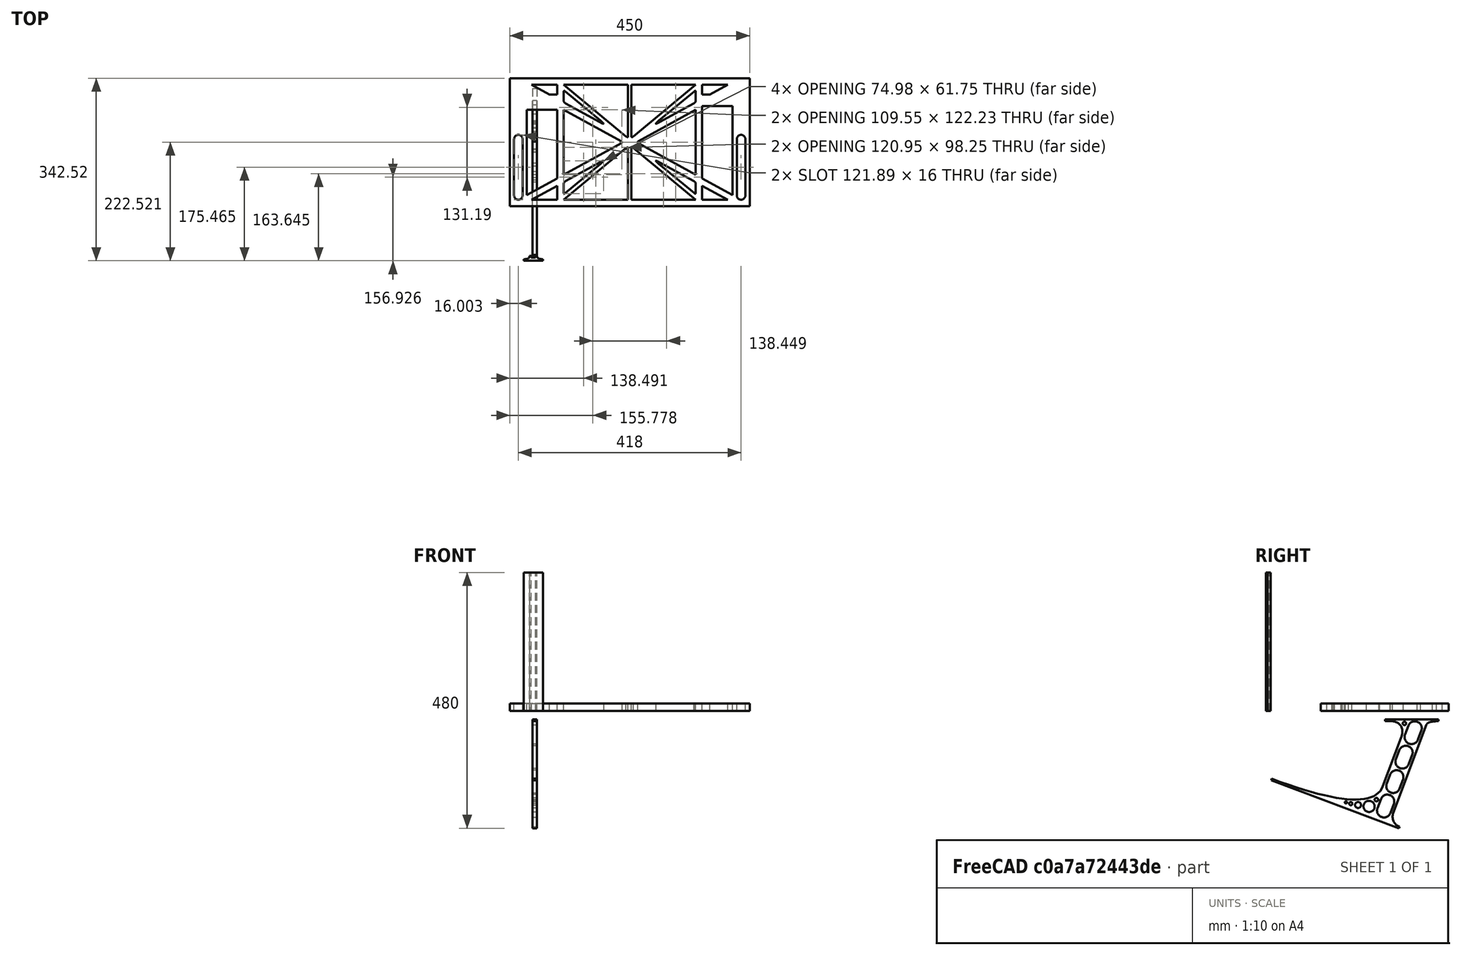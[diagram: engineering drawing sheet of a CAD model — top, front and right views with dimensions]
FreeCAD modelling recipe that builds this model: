
FCSTD DOCUMENT  (FreeCAD 0.19R0.19.2)
Label: laptopStand076
License: All rights reserved
LicenseURL: http://en.wikipedia.org/wiki/All_rights_reserved
objects: Sketcher::SketchObject×3, Part::Extrusion×3
note: 6 computed .brp shape members not serialized (recipe doc carries the construction recipe); baked Part::Feature solids carry a one-line shape summary decoded from their .brp

FEATURE [Sketcher::SketchObject] Sketch
  FullyConstrained = false
  sketch-geometry (176):
    g0: LineSegment StartX=-10.9272 StartY=-82.7794 StartZ=0 EndX=46.0728 EndY=-51.4823 EndZ=0
    g1: LineSegment StartX=366.073 StartY=-91.7794 StartZ=0 EndX=318.073 EndY=-65.424 EndZ=0
    g2: LineSegment StartX=-10.9272 StartY=77.3346 StartZ=0 EndX=-10.9272 EndY=-82.7794 EndZ=0
    g3: LineSegment StartX=375.073 StartY=-82.7794 StartZ=0 EndX=375.073 EndY=83.9235 EndZ=0
    g4: LineSegment StartX=-1.92719 StartY=-91.7794 StartZ=0 EndX=46.0728 EndY=-91.7794 EndZ=0
    g5: LineSegment StartX=318.073 StartY=124.221 StartZ=0 EndX=366.073 EndY=124.221 EndZ=0
    g6: LineSegment StartX=306.073 StartY=124.221 StartZ=0 EndX=189.124 EndY=27.0628 EndZ=0
    g7: LineSegment StartX=58.0728 StartY=-91.7794 StartZ=0 EndX=175.022 EndY=5.37834 EndZ=0
    g8: LineSegment StartX=175.022 StartY=27.0628 StartZ=0 EndX=58.0728 EndY=124.221 EndZ=0
    g9: LineSegment StartX=189.124 StartY=5.37834 StartZ=0 EndX=306.073 EndY=-91.7794 EndZ=0
    g10: LineSegment StartX=306.073 StartY=77.3346 StartZ=0 EndX=306.073 EndY=-44.8935 EndZ=0
    g11: LineSegment StartX=318.073 StartY=83.9235 StartZ=0 EndX=318.073 EndY=-51.4823 EndZ=0
    g12: LineSegment StartX=306.073 StartY=-58.8351 StartZ=0 EndX=306.073 EndY=-81.8102 EndZ=0
    g13: LineSegment StartX=318.073 StartY=-51.4823 StartZ=0 EndX=375.073 EndY=-82.7794 EndZ=0
    g14: LineSegment StartX=318.073 StartY=-65.424 StartZ=0 EndX=318.073 EndY=-91.7794 EndZ=0
    g15: LineSegment StartX=318.073 StartY=-91.7794 StartZ=0 EndX=366.073 EndY=-91.7794 EndZ=0
    g16: LineSegment StartX=58.0728 StartY=-44.8935 StartZ=0 EndX=58.0728 EndY=77.3346 EndZ=0
    g17: LineSegment StartX=46.0728 StartY=-65.424 StartZ=0 EndX=-1.92719 EndY=-91.7794 EndZ=0
    g18: LineSegment StartX=46.0728 StartY=-65.424 StartZ=0 EndX=46.0728 EndY=-91.7794 EndZ=0
    g19: LineSegment StartX=46.0728 StartY=77.3346 StartZ=0 EndX=46.0728 EndY=-51.4823 EndZ=0
    g20: LineSegment StartX=-42.9272 StartY=136.221 StartZ=0 EndX=-42.9272 EndY=-103.779 EndZ=0
    g21: LineSegment StartX=407.073 StartY=136.221 StartZ=0 EndX=407.073 EndY=-103.779 EndZ=0
    g22: LineSegment StartX=179.022 StartY=27.0628 StartZ=0 EndX=179.022 EndY=124.221 EndZ=0
    g23: LineSegment StartX=185.124 StartY=27.0628 StartZ=0 EndX=185.124 EndY=124.221 EndZ=0
    g24: ArcOfCircle CenterX=-26.9272 CenterY=22.1087 CenterZ=0 NormalX=0 NormalY=0 NormalZ=1 AngleXU=0 Radius=8 StartAngle=1e-16 EndAngle=3.14159
    g25: ArcOfCircle CenterX=-26.9272 CenterY=-83.7794 CenterZ=0 NormalX=0 NormalY=0 NormalZ=1 AngleXU=0 Radius=8 StartAngle=3.14159 EndAngle=6.28319
    g26: LineSegment StartX=-34.9272 StartY=22.1087 StartZ=0 EndX=-34.9272 EndY=-83.7794 EndZ=0
    g27: LineSegment StartX=-18.9272 StartY=22.1087 StartZ=0 EndX=-18.9272 EndY=-83.7794 EndZ=0
    g28: LineSegment StartX=185.124 StartY=-91.7794 StartZ=0 EndX=306.073 EndY=-91.7794 EndZ=0
    g29: LineSegment StartX=179.022 StartY=-91.7794 StartZ=0 EndX=58.0728 EndY=-91.7794 EndZ=0
    g30: LineSegment StartX=306.073 StartY=124.221 StartZ=0 EndX=185.124 EndY=124.221 EndZ=0
    g31: LineSegment StartX=179.022 StartY=124.221 StartZ=0 EndX=58.0728 EndY=124.221 EndZ=0
    g32: ArcOfCircle CenterX=391.073 CenterY=22.1087 CenterZ=0 NormalX=0 NormalY=0 NormalZ=1 AngleXU=0 Radius=8 StartAngle=-4.4e-15 EndAngle=3.14159
    g33: LineSegment StartX=399.073 StartY=22.1087 StartZ=0 EndX=399.073 EndY=-83.7794 EndZ=0
    g34: LineSegment StartX=383.073 StartY=22.1087 StartZ=0 EndX=383.073 EndY=-83.7794 EndZ=0
    g35: ArcOfCircle CenterX=391.073 CenterY=-83.7794 CenterZ=0 NormalX=0 NormalY=0 NormalZ=1 AngleXU=0 Radius=8 StartAngle=3.14159 EndAngle=6.28319
    g36: Circle CenterX=175.022 CenterY=27.0628 CenterZ=0 NormalX=0 NormalY=0 NormalZ=1 AngleXU=0 Radius=1
    g37: Circle CenterX=179.022 CenterY=24.8665 CenterZ=0 NormalX=0 NormalY=0 NormalZ=1 AngleXU=0 Radius=1
    g38: Circle CenterX=179.022 CenterY=27.0628 CenterZ=0 NormalX=0 NormalY=0 NormalZ=1 AngleXU=0 Radius=1
    g39: BSplineCurve PolesCount=3 KnotsCount=2 Degree=2 IsPeriodic=0
    g40: GeomPoint X=175.022 Y=27.0628 Z=0
    g41: GeomPoint X=179.022 Y=27.0628 Z=0
    g42: Circle CenterX=189.124 CenterY=27.0628 CenterZ=0 NormalX=0 NormalY=0 NormalZ=1 AngleXU=0 Radius=1
    g43: Circle CenterX=185.124 CenterY=24.8665 CenterZ=0 NormalX=0 NormalY=0 NormalZ=1 AngleXU=0 Radius=1
    g44: Circle CenterX=185.124 CenterY=27.0628 CenterZ=0 NormalX=0 NormalY=0 NormalZ=1 AngleXU=0 Radius=1
    g45: BSplineCurve PolesCount=3 KnotsCount=2 Degree=2 IsPeriodic=0
    g46: GeomPoint X=189.124 Y=27.0628 Z=0
    g47: GeomPoint X=185.124 Y=27.0628 Z=0
    g48: Circle CenterX=175.022 CenterY=5.37834 CenterZ=0 NormalX=0 NormalY=0 NormalZ=1 AngleXU=0 Radius=1
    g49: Circle CenterX=179.022 CenterY=7.57463 CenterZ=0 NormalX=0 NormalY=0 NormalZ=1 AngleXU=0 Radius=1
    g50: Circle CenterX=179.022 CenterY=5.34704 CenterZ=0 NormalX=0 NormalY=0 NormalZ=1 AngleXU=0 Radius=1
    g51: BSplineCurve PolesCount=3 KnotsCount=2 Degree=2 IsPeriodic=0
    g52: GeomPoint X=175.022 Y=5.37834 Z=0
    g53: GeomPoint X=179.022 Y=5.34704 Z=0
    g54: Circle CenterX=189.124 CenterY=5.37834 CenterZ=0 NormalX=0 NormalY=0 NormalZ=1 AngleXU=0 Radius=1
    g55: Circle CenterX=185.124 CenterY=7.57463 CenterZ=0 NormalX=0 NormalY=0 NormalZ=1 AngleXU=0 Radius=1
    g56: Circle CenterX=185.124 CenterY=5.34704 CenterZ=0 NormalX=0 NormalY=0 NormalZ=1 AngleXU=0 Radius=1
    g57: BSplineCurve PolesCount=3 KnotsCount=2 Degree=2 IsPeriodic=0
    g58: GeomPoint X=189.124 Y=5.37834 Z=0
    g59: GeomPoint X=185.124 Y=5.34704 Z=0
    g60: LineSegment StartX=179.022 StartY=5.34704 StartZ=0 EndX=179.022 EndY=-91.7794 EndZ=0
    g61: LineSegment StartX=185.124 StartY=-91.7794 StartZ=0 EndX=185.124 EndY=5.34704 EndZ=0
    g62: Circle CenterX=165.871 CenterY=18.1458 CenterZ=0 NormalX=0 NormalY=0 NormalZ=1 AngleXU=0 Radius=1
    g63: Circle CenterX=169.377 CenterY=16.2206 CenterZ=0 NormalX=0 NormalY=0 NormalZ=1 AngleXU=0 Radius=1
    g64: Circle CenterX=165.871 CenterY=14.2954 CenterZ=0 NormalX=0 NormalY=0 NormalZ=1 AngleXU=0 Radius=1
    g65: BSplineCurve PolesCount=3 KnotsCount=2 Degree=2 IsPeriodic=0
    g66: GeomPoint X=165.871 Y=18.1458 Z=0
    g67: GeomPoint X=165.871 Y=14.2954 Z=0
    g68: Circle CenterX=198.275 CenterY=18.1458 CenterZ=0 NormalX=0 NormalY=0 NormalZ=1 AngleXU=0 Radius=1
    g69: Circle CenterX=194.768 CenterY=16.2206 CenterZ=0 NormalX=0 NormalY=0 NormalZ=1 AngleXU=0 Radius=1
    g70: Circle CenterX=198.275 CenterY=14.2954 CenterZ=0 NormalX=0 NormalY=0 NormalZ=1 AngleXU=0 Radius=1
    g71: BSplineCurve PolesCount=3 KnotsCount=2 Degree=2 IsPeriodic=0
    g72: GeomPoint X=198.275 Y=18.1458 Z=0
    g73: GeomPoint X=198.275 Y=14.2954 Z=0
    g74: LineSegment StartX=165.871 StartY=18.1458 StartZ=0 EndX=58.0728 EndY=77.3346 EndZ=0
    g75: LineSegment StartX=58.0728 StartY=-44.8935 StartZ=0 EndX=165.871 EndY=14.2954 EndZ=0
    g76: LineSegment StartX=198.275 StartY=18.1458 StartZ=0 EndX=306.073 EndY=77.3346 EndZ=0
    g77: LineSegment StartX=198.275 StartY=14.2954 StartZ=0 EndX=306.073 EndY=-44.8935 EndZ=0
    g78: LineSegment StartX=407.073 StartY=-103.779 StartZ=0 EndX=-42.9272 EndY=-103.779 EndZ=0
    g79: LineSegment StartX=407.073 StartY=136.221 StartZ=0 EndX=-42.9272 EndY=136.221 EndZ=0
    g80: LineSegment StartX=46.0728 StartY=77.3346 StartZ=0 EndX=-10.9272 EndY=77.3346 EndZ=0
    g81: LineSegment StartX=46.0728 StartY=105.865 StartZ=0 EndX=31.5028 EndY=105.865 EndZ=0
    g82: LineSegment StartX=46.0728 StartY=124.221 StartZ=0 EndX=46.0728 EndY=105.865 EndZ=0
    g83: LineSegment StartX=-1.92719 StartY=124.221 StartZ=0 EndX=31.5028 EndY=105.865 EndZ=0
    g84: LineSegment StartX=46.0728 StartY=124.221 StartZ=0 EndX=-1.92719 EndY=124.221 EndZ=0
    g85: LineSegment StartX=318.073 StartY=83.9235 StartZ=0 EndX=375.073 EndY=83.9235 EndZ=0
    g86: LineSegment StartX=318.073 StartY=105.865 StartZ=0 EndX=332.643 EndY=105.865 EndZ=0
    g87: LineSegment StartX=332.643 StartY=105.865 StartZ=0 EndX=366.073 EndY=124.221 EndZ=0
    g88: LineSegment StartX=318.073 StartY=124.221 StartZ=0 EndX=318.073 EndY=105.865 EndZ=0
    g89: Circle CenterX=125.607 CenterY=54.1951 CenterZ=0 NormalX=0 NormalY=0 NormalZ=1 AngleXU=0 Radius=1
    g90: Circle CenterX=139.632 CenterY=46.4944 CenterZ=0 NormalX=0 NormalY=0 NormalZ=1 AngleXU=0 Radius=1
    g91: Circle CenterX=127.326 CenterY=56.7187 CenterZ=0 NormalX=0 NormalY=0 NormalZ=1 AngleXU=0 Radius=1
    g92: BSplineCurve PolesCount=3 KnotsCount=2 Degree=2 IsPeriodic=0
    g93: GeomPoint X=125.607 Y=54.1951 Z=0
    g94: GeomPoint X=127.326 Y=56.7187 Z=0
    g95: Circle CenterX=236.821 CenterY=56.7187 CenterZ=0 NormalX=0 NormalY=0 NormalZ=1 AngleXU=0 Radius=1
    g96: Circle CenterX=224.513 CenterY=46.4944 CenterZ=0 NormalX=0 NormalY=0 NormalZ=1 AngleXU=0 Radius=1
    g97: Circle CenterX=238.538 CenterY=54.1951 CenterZ=0 NormalX=0 NormalY=0 NormalZ=1 AngleXU=0 Radius=1
    g98: BSplineCurve PolesCount=3 KnotsCount=2 Degree=2 IsPeriodic=0
    g99: GeomPoint X=236.821 Y=56.7187 Z=0
    g100: GeomPoint X=238.538 Y=54.1951 Z=0
    g101: Circle CenterX=238.538 CenterY=-21.7539 CenterZ=0 NormalX=0 NormalY=0 NormalZ=1 AngleXU=0 Radius=1
    g102: Circle CenterX=224.513 CenterY=-14.0532 CenterZ=0 NormalX=0 NormalY=0 NormalZ=1 AngleXU=0 Radius=1
    g103: Circle CenterX=236.821 CenterY=-24.2775 CenterZ=0 NormalX=0 NormalY=0 NormalZ=1 AngleXU=0 Radius=1
    g104: BSplineCurve PolesCount=3 KnotsCount=2 Degree=2 IsPeriodic=0
    g105: GeomPoint X=238.538 Y=-21.7539 Z=0
    g106: GeomPoint X=236.821 Y=-24.2775 Z=0
    g107: LineSegment StartX=238.538 StartY=-21.7539 StartZ=0 EndX=306.073 EndY=-58.8351 EndZ=0
    g108: LineSegment StartX=236.821 StartY=-24.2775 StartZ=0 EndX=306.073 EndY=-81.8102 EndZ=0
    g109: Circle CenterX=125.607 CenterY=-21.7539 CenterZ=0 NormalX=0 NormalY=0 NormalZ=1 AngleXU=0 Radius=1
    g110: Circle CenterX=139.632 CenterY=-14.0532 CenterZ=0 NormalX=0 NormalY=0 NormalZ=1 AngleXU=0 Radius=1
    g111: Circle CenterX=127.325 CenterY=-24.2775 CenterZ=0 NormalX=0 NormalY=0 NormalZ=1 AngleXU=0 Radius=1
    g112: BSplineCurve PolesCount=3 KnotsCount=2 Degree=2 IsPeriodic=0
    g113: GeomPoint X=125.607 Y=-21.7539 Z=0
    g114: GeomPoint X=127.325 Y=-24.2775 Z=0
    g115: Circle CenterX=302.996 CenterY=111.695 CenterZ=0 NormalX=0 NormalY=0 NormalZ=1 AngleXU=0 Radius=1
    g116: Circle CenterX=306.073 CenterY=114.251 CenterZ=0 NormalX=0 NormalY=0 NormalZ=1 AngleXU=0 Radius=1
    g117: Circle CenterX=306.073 CenterY=110.251 CenterZ=0 NormalX=0 NormalY=0 NormalZ=1 AngleXU=0 Radius=1
    g118: BSplineCurve PolesCount=3 KnotsCount=2 Degree=2 IsPeriodic=0
    g119: GeomPoint X=302.996 Y=111.695 Z=0
    g120: GeomPoint X=306.073 Y=110.251 Z=0
    g121: Circle CenterX=306.073 CenterY=95.2763 CenterZ=0 NormalX=0 NormalY=0 NormalZ=1 AngleXU=0 Radius=1
    g122: Circle CenterX=306.073 CenterY=91.2763 CenterZ=0 NormalX=0 NormalY=0 NormalZ=1 AngleXU=0 Radius=1
    g123: Circle CenterX=302.567 CenterY=89.3511 CenterZ=0 NormalX=0 NormalY=0 NormalZ=1 AngleXU=0 Radius=1
    g124: BSplineCurve PolesCount=3 KnotsCount=2 Degree=2 IsPeriodic=0
    g125: GeomPoint X=306.073 Y=95.2763 Z=0
    g126: GeomPoint X=302.567 Y=89.3511 Z=0
    g127: LineSegment StartX=306.073 StartY=110.251 StartZ=0 EndX=306.073 EndY=95.2763 EndZ=0
    g128: LineSegment StartX=302.996 StartY=111.695 StartZ=0 EndX=236.821 EndY=56.7187 EndZ=0
    g129: LineSegment StartX=238.538 StartY=54.1951 StartZ=0 EndX=302.567 EndY=89.3511 EndZ=0
    g130: Circle CenterX=61.1496 CenterY=111.695 CenterZ=0 NormalX=0 NormalY=0 NormalZ=1 AngleXU=0 Radius=1
    g131: Circle CenterX=58.0728 CenterY=114.251 CenterZ=0 NormalX=0 NormalY=0 NormalZ=1 AngleXU=0 Radius=1
    g132: Circle CenterX=58.0728 CenterY=110.251 CenterZ=0 NormalX=0 NormalY=0 NormalZ=1 AngleXU=0 Radius=1
    g133: BSplineCurve PolesCount=3 KnotsCount=2 Degree=2 IsPeriodic=0
    g134: GeomPoint X=61.1496 Y=111.695 Z=0
    g135: GeomPoint X=58.0728 Y=110.251 Z=0
    g136: Circle CenterX=61.5791 CenterY=89.3511 CenterZ=0 NormalX=0 NormalY=0 NormalZ=1 AngleXU=0 Radius=1
    g137: Circle CenterX=58.0728 CenterY=91.2763 CenterZ=0 NormalX=0 NormalY=0 NormalZ=1 AngleXU=0 Radius=1
    g138: Circle CenterX=58.0728 CenterY=95.2763 CenterZ=0 NormalX=0 NormalY=0 NormalZ=1 AngleXU=0 Radius=1
    g139: BSplineCurve PolesCount=3 KnotsCount=2 Degree=2 IsPeriodic=0
    g140: GeomPoint X=61.5791 Y=89.3511 Z=0
    g141: GeomPoint X=58.0728 Y=95.2763 Z=0
    g142: LineSegment StartX=58.0728 StartY=110.251 StartZ=0 EndX=58.0728 EndY=95.2763 EndZ=0
    g143: LineSegment StartX=61.1496 StartY=111.695 StartZ=0 EndX=127.326 EndY=56.7187 EndZ=0
    g144: LineSegment StartX=125.607 StartY=54.1951 StartZ=0 EndX=61.5791 EndY=89.3511 EndZ=0
    g145: Circle CenterX=61.5791 CenterY=-56.9099 CenterZ=0 NormalX=0 NormalY=0 NormalZ=1 AngleXU=0 Radius=1
    g146: Circle CenterX=58.0728 CenterY=-58.8351 CenterZ=0 NormalX=0 NormalY=0 NormalZ=1 AngleXU=0 Radius=1
    g147: Circle CenterX=58.0728 CenterY=-62.8351 CenterZ=0 NormalX=0 NormalY=0 NormalZ=1 AngleXU=0 Radius=1
    g148: BSplineCurve PolesCount=3 KnotsCount=2 Degree=2 IsPeriodic=0
    g149: GeomPoint X=61.5791 Y=-56.9099 Z=0
    g150: GeomPoint X=58.0728 Y=-62.8351 Z=0
    g151: Circle CenterX=58.0728 CenterY=-77.8102 CenterZ=0 NormalX=0 NormalY=0 NormalZ=1 AngleXU=0 Radius=1
    g152: Circle CenterX=58.0728 CenterY=-81.8102 CenterZ=0 NormalX=0 NormalY=0 NormalZ=1 AngleXU=0 Radius=1
    g153: Circle CenterX=61.1496 CenterY=-79.2541 CenterZ=0 NormalX=0 NormalY=0 NormalZ=1 AngleXU=0 Radius=1
    g154: BSplineCurve PolesCount=3 KnotsCount=2 Degree=2 IsPeriodic=0
    g155: GeomPoint X=58.0728 Y=-77.8102 Z=0
    g156: GeomPoint X=61.1496 Y=-79.2541 Z=0
    g157: LineSegment StartX=58.0728 StartY=-62.8351 StartZ=0 EndX=58.0728 EndY=-77.8102 EndZ=0
    g158: LineSegment StartX=61.1496 StartY=-79.2541 StartZ=0 EndX=127.325 EndY=-24.2775 EndZ=0
    g159: LineSegment StartX=125.607 StartY=-21.7539 StartZ=0 EndX=61.5791 EndY=-56.9099 EndZ=0
    g160: LineSegment StartX=306.073 StartY=-58.8351 StartZ=0 EndX=302.567 EndY=-56.9099 EndZ=0
    g161: LineSegment StartX=306.073 StartY=-58.8351 StartZ=0 EndX=306.073 EndY=-62.8351 EndZ=0
    g162: LineSegment StartX=306.073 StartY=-81.8102 StartZ=0 EndX=306.073 EndY=-77.8102 EndZ=0
    g163: LineSegment StartX=306.073 StartY=-81.8102 StartZ=0 EndX=302.996 EndY=-79.2541 EndZ=0
    g164: Circle CenterX=302.567 CenterY=-56.9099 CenterZ=0 NormalX=0 NormalY=0 NormalZ=1 AngleXU=0 Radius=1
    g165: Circle CenterX=306.073 CenterY=-58.8351 CenterZ=0 NormalX=0 NormalY=0 NormalZ=1 AngleXU=0 Radius=1
    g166: Circle CenterX=306.073 CenterY=-62.8351 CenterZ=0 NormalX=0 NormalY=0 NormalZ=1 AngleXU=0 Radius=1
    g167: BSplineCurve PolesCount=3 KnotsCount=2 Degree=2 IsPeriodic=0
    g168: GeomPoint X=302.567 Y=-56.9099 Z=0
    g169: GeomPoint X=306.073 Y=-62.8351 Z=0
    g170: Circle CenterX=302.996 CenterY=-79.2541 CenterZ=0 NormalX=0 NormalY=0 NormalZ=1 AngleXU=0 Radius=1
    g171: Circle CenterX=306.073 CenterY=-81.8102 CenterZ=0 NormalX=0 NormalY=0 NormalZ=1 AngleXU=0 Radius=1
    g172: Circle CenterX=306.073 CenterY=-77.8102 CenterZ=0 NormalX=0 NormalY=0 NormalZ=1 AngleXU=0 Radius=1
    g173: BSplineCurve PolesCount=3 KnotsCount=2 Degree=2 IsPeriodic=0
    g174: GeomPoint X=302.996 Y=-79.2541 Z=0
    g175: GeomPoint X=306.073 Y=-77.8102 Z=0
  constraints (316):
    c: Horizontal(g4)
    c: Horizontal(g5)
    c: Coincident(g11,g13)
    c: Coincident(g14,g1)
    c: Tangent(g11,g14)
    c: Coincident(g18,g17)
    c: Coincident(g0,g19)
    c: Block(g8)
    c: Block(g6)
    c: Block(g13)
    c: Block(g3)
    c: Block(g12)
    c: Block(g1)
    c: Block(g14)
    c: Block(g9)
    c: Block(g7)
    c: Block(g18)
    c: Block(g17)
    c: Block(g0)
    c: Block(g2)
    c: Block(g10)
    c: Block(g5)
    c: Block(g15)
    c: Block(g4)
    c: Vertical(g20)
    c: Vertical(g21)
    c: Block(g21)
    c: Block(g20)
    c: Vertical(g22)
    c: Vertical(g23)
    c: Block(g22)
    c: Block(g23)
    c: Tangent(g24,g27) = 1.5708
    c: Tangent(g24,g26) = -1.5708
    c: Tangent(g26,g25) = -1.5708
    c: Tangent(g27,g25) = 1.5708
    c: Vertical(g26)
    c: Equal(g24,g25)
    c: Block(g27)
    c: Block(g26)
    c: Coincident(g28,g9)
    c: Horizontal(g28)
    c: Coincident(g29,g7)
    c: Horizontal(g29)
    c: Coincident(g30,g6)
    c: Coincident(g30,g23)
    c: Horizontal(g30)
    c: Coincident(g31,g22)
    c: Coincident(g31,g8)
    c: Horizontal(g31)
    c: Tangent(g32,g33) = 1.5708
    c: Tangent(g33,g35) = 1.5708
    c: Equal(g32,g35)
    c: Coincident(g34,g32)
    c: Coincident(g34,g35)
    c: Block(g33)
    c: Block(g34)
    c: Coincident(g39,g8)
    c: Weight(g36) = 1
    c: Equal(g36,g37)
    c: Equal(g36,g38)
    c: Coincident(g39,g22)
    c: InternalAlignment(g36,g39)
    c: InternalAlignment(g37,g39)
    c: InternalAlignment(g38,g39)
    c: InternalAlignment(g40,g39)
    c: InternalAlignment(g41,g39)
    c: Coincident(g45,g6)
    c: Weight(g42) = 1
    c: Equal(g42,g43)
    c: Equal(g42,g44)
    c: Coincident(g45,g23)
    c: InternalAlignment(g42,g45)
    c: InternalAlignment(g43,g45)
    c: InternalAlignment(g44,g45)
    c: InternalAlignment(g46,g45)
    c: InternalAlignment(g47,g45)
    c: Block(g45)
    c: Block(g39)
    c: Coincident(g51,g7)
    c: Weight(g48) = 1
    c: Equal(g48,g49)
    c: Equal(g48,g50)
    c: InternalAlignment(g48,g51)
    c: InternalAlignment(g49,g51)
    c: InternalAlignment(g50,g51)
    c: InternalAlignment(g52,g51)
    c: InternalAlignment(g53,g51)
    c: Weight(g54) = 1
    c: Equal(g54,g55)
    c: Equal(g54,g56)
    c: InternalAlignment(g54,g57)
    c: InternalAlignment(g55,g57)
    c: InternalAlignment(g56,g57)
    c: InternalAlignment(g58,g57)
    c: InternalAlignment(g59,g57)
    c: Block(g57)
    c: Block(g51)
    c: Coincident(g60,g51)
    c: Coincident(g60,g29)
    c: Vertical(g60)
    c: Coincident(g61,g28)
    c: Coincident(g61,g57)
    c: Vertical(g61)
    c: Weight(g62) = 1
    c: Equal(g62,g63)
    c: Equal(g62,g64)
    c: InternalAlignment(g62,g65)
    c: InternalAlignment(g63,g65)
    c: InternalAlignment(g64,g65)
    c: InternalAlignment(g66,g65)
    c: InternalAlignment(g67,g65)
    c: Weight(g68) = 1
    c: Equal(g68,g69)
    c: Equal(g68,g70)
    c: InternalAlignment(g68,g71)
    c: InternalAlignment(g69,g71)
    c: InternalAlignment(g70,g71)
    c: InternalAlignment(g72,g71)
    c: InternalAlignment(g73,g71)
    c: Block(g65)
    c: Block(g71)
    c: Coincident(g74,g65)
    c: Coincident(g74,g16)
    c: Coincident(g75,g16)
    c: Coincident(g75,g65)
    c: Coincident(g76,g71)
    c: Coincident(g76,g10)
    c: Coincident(g77,g71)
    c: Coincident(g77,g10)
    c: Block(g16)
    c: Coincident(g78,g21)
    c: Coincident(g78,g20)
    c: Horizontal(g78)
    c: Distance(g78) = 450
    c: Coincident(g79,g21)
    c: Coincident(g79,g20)
    c: Horizontal(g79)
    c: Horizontal(g80)
    c: Coincident(g19,g80)
    c: Horizontal(g81)
    c: Vertical(g82)
    c: Block(g82)
    c: Block(g81)
    c: Block(g80)
    c: Distance(g82) = 18.3554
    c: Coincident(g84,g82)
    c: Coincident(g84,g83)
    c: Horizontal(g84)
    c: Block(g84)
    c: Block(g83)
    c: Coincident(g81,g83)
    c: Coincident(g2,g80)
    c: Coincident(g85,g11)
    c: Horizontal(g85)
    c: Horizontal(g86)
    c: Block(g85)
    c: Coincident(g87,g5)
    c: Coincident(g88,g5)
    c: Coincident(g88,g86)
    c: Vertical(g88)
    c: Block(g88)
    c: Coincident(g86,g87)
    c: Block(g87)
    c: Coincident(g3,g85)
    c: Weight(g89) = 1
    c: Equal(g89,g90)
    c: Equal(g89,g91)
    c: InternalAlignment(g89,g92)
    c: InternalAlignment(g90,g92)
    c: InternalAlignment(g91,g92)
    c: InternalAlignment(g93,g92)
    c: InternalAlignment(g94,g92)
    c: Block(g92)
    c: Weight(g95) = 1
    c: Equal(g95,g96)
    c: Equal(g95,g97)
    c: InternalAlignment(g95,g98)
    c: InternalAlignment(g96,g98)
    c: InternalAlignment(g97,g98)
    c: InternalAlignment(g99,g98)
    c: InternalAlignment(g100,g98)
    c: Block(g98)
    c: Weight(g101) = 1
    c: Equal(g101,g102)
    c: Equal(g101,g103)
    c: InternalAlignment(g101,g104)
    c: InternalAlignment(g102,g104)
    c: InternalAlignment(g103,g104)
    c: InternalAlignment(g105,g104)
    c: InternalAlignment(g106,g104)
    c: Block(g104)
    c: Coincident(g107,g104)
    c: Coincident(g107,g12)
    c: Coincident(g108,g104)
    c: Coincident(g108,g12)
    c: Weight(g109) = 1
    c: Equal(g109,g110)
    c: Equal(g109,g111)
    c: InternalAlignment(g109,g112)
    c: InternalAlignment(g110,g112)
    c: InternalAlignment(g111,g112)
    c: InternalAlignment(g113,g112)
    c: InternalAlignment(g114,g112)
    c: Block(g112)
    c: Weight(g115) = 1
    c: Equal(g115,g116)
    c: Equal(g115,g117)
    c: InternalAlignment(g115,g118)
    c: InternalAlignment(g116,g118)
    c: InternalAlignment(g117,g118)
    c: InternalAlignment(g119,g118)
    c: InternalAlignment(g120,g118)
    c: Weight(g121) = 1
    c: Equal(g121,g122)
    c: Equal(g121,g123)
    c: InternalAlignment(g121,g124)
    c: InternalAlignment(g122,g124)
    c: InternalAlignment(g123,g124)
    c: InternalAlignment(g125,g124)
    c: InternalAlignment(g126,g124)
    c: Block(g118)
    c: Block(g124)
    c: Coincident(g127,g118)
    c: Coincident(g127,g124)
    c: Vertical(g127)
    c: Coincident(g128,g118)
    c: Coincident(g128,g98)
    c: Coincident(g129,g98)
    c: Coincident(g129,g124)
    c: Weight(g130) = 1
    c: Equal(g130,g131)
    c: Equal(g130,g132)
    c: InternalAlignment(g130,g133)
    c: InternalAlignment(g131,g133)
    c: InternalAlignment(g132,g133)
    c: InternalAlignment(g134,g133)
    c: InternalAlignment(g135,g133)
    c: Weight(g136) = 1
    c: Equal(g136,g137)
    c: Equal(g136,g138)
    c: InternalAlignment(g136,g139)
    c: InternalAlignment(g137,g139)
    c: InternalAlignment(g138,g139)
    c: InternalAlignment(g140,g139)
    c: InternalAlignment(g141,g139)
    c: Block(g133)
    c: Block(g139)
    c: Coincident(g142,g133)
    c: Coincident(g142,g139)
    c: Vertical(g142)
    c: Coincident(g143,g133)
    c: Coincident(g143,g92)
    c: Coincident(g144,g92)
    c: Coincident(g144,g139)
    c: Weight(g145) = 1
    c: Equal(g145,g146)
    c: Equal(g145,g147)
    c: InternalAlignment(g145,g148)
    c: InternalAlignment(g146,g148)
    c: InternalAlignment(g147,g148)
    c: InternalAlignment(g149,g148)
    c: InternalAlignment(g150,g148)
    c: Weight(g151) = 1
    c: Equal(g151,g152)
    c: Equal(g151,g153)
    c: InternalAlignment(g151,g154)
    c: InternalAlignment(g152,g154)
    c: InternalAlignment(g153,g154)
    c: InternalAlignment(g155,g154)
    c: InternalAlignment(g156,g154)
    c: Block(g148)
    c: Block(g154)
    c: Coincident(g157,g148)
    c: Coincident(g157,g154)
    c: Vertical(g157)
    c: Coincident(g158,g154)
    c: Coincident(g158,g112)
    c: Coincident(g159,g112)
    c: Coincident(g159,g148)
    c: Vertical(g161)
    c: Vertical(g162)
    c: Distance(g160) = 4
    c: Distance(g161) = 4
    c: Distance(g162) = 4
    c: Distance(g163) = 4
    c: Parallel(g160,g107)
    c: Parallel(g163,g108)
    c: Coincident(g161,g12)
    c: Coincident(g160,g12)
    c: Coincident(g162,g12)
    c: Coincident(g163,g12)
    c: Coincident(g167,g160)
    c: Weight(g164) = 1
    c: Equal(g164,g165)
    c: Coincident(g165,g12)
    c: Equal(g164,g166)
    c: Coincident(g167,g161)
    c: InternalAlignment(g164,g167)
    c: InternalAlignment(g165,g167)
    c: InternalAlignment(g166,g167)
    c: InternalAlignment(g168,g167)
    c: InternalAlignment(g169,g167)
    c: Coincident(g173,g163)
    c: Weight(g170) = 1
    c: Equal(g170,g171)
    c: Coincident(g171,g12)
    c: Equal(g170,g172)
    c: Coincident(g173,g162)
    c: InternalAlignment(g170,g173)
    c: InternalAlignment(g171,g173)
    c: InternalAlignment(g172,g173)
    c: InternalAlignment(g174,g173)
    c: InternalAlignment(g175,g173)
    c: Block(g167)
    c: Block(g173)
FEATURE [Sketcher::SketchObject] Sketch001
  FullyConstrained = true
  MapMode = 4
  Placement = pos=(0,0,0) rot=(0.57735,0.57735,0.57735;2.0944rad)
  Support = -> [Sketch]
  sketch-geometry (46):
    g0: BSplineCurve PolesCount=3 KnotsCount=2 Degree=2 IsPeriodic=0
    g1: ArcOfCircle CenterX=73.1223 CenterY=-32.291 CenterZ=0 NormalX=0 NormalY=0 NormalZ=1 AngleXU=0 Radius=13 StartAngle=5.92268 EndAngle=9.06428
    g2: ArcOfCircle CenterX=66.7816 CenterY=-49.1439 CenterZ=0 NormalX=0 NormalY=0 NormalZ=1 AngleXU=0 Radius=13 StartAngle=2.78068 EndAngle=5.92131
    g3: ArcOfCircle CenterX=55.9263 CenterY=-78.1807 CenterZ=0 NormalX=0 NormalY=0 NormalZ=1 AngleXU=0 Radius=13 StartAngle=5.92268 EndAngle=9.06428
    g4: ArcOfCircle CenterX=49.5884 CenterY=-95.0342 CenterZ=0 NormalX=0 NormalY=0 NormalZ=1 AngleXU=0 Radius=13 StartAngle=2.78068 EndAngle=5.92131
    g5: ArcOfCircle CenterX=38.7206 CenterY=-124.067 CenterZ=0 NormalX=0 NormalY=0 NormalZ=1 AngleXU=0 Radius=13 StartAngle=5.92268 EndAngle=9.06428
    g6: ArcOfCircle CenterX=32.3875 CenterY=-140.92 CenterZ=0 NormalX=0 NormalY=0 NormalZ=1 AngleXU=0 Radius=13 StartAngle=2.78068 EndAngle=5.92131
    g7: ArcOfCircle CenterX=21.4715 CenterY=-169.934 CenterZ=0 NormalX=0 NormalY=0 NormalZ=1 AngleXU=0 Radius=13 StartAngle=5.92268 EndAngle=9.06428
    g8: ArcOfCircle CenterX=15.1336 CenterY=-186.787 CenterZ=0 NormalX=0 NormalY=0 NormalZ=1 AngleXU=0 Radius=13 StartAngle=2.78068 EndAngle=5.92131
    g9-g12: Circle x4 (B-spline internal-alignment scaffolding for g13; pole/knot coordinates omitted)
    g13: BSplineCurve PolesCount=4 KnotsCount=2 Degree=3 IsPeriodic=0
    g14: GeomPoint X=28.8094 Y=-19.0875 Z=0
    g15: GeomPoint X=47.0443 Y=-50.4712 Z=0
    g16: Circle CenterX=53.5586 CenterY=-23.2695 CenterZ=0 NormalX=0 NormalY=0 NormalZ=1 AngleXU=0 Radius=3.24518
    g17: Circle CenterX=-195.441 CenterY=-127.082 CenterZ=0 NormalX=0 NormalY=0 NormalZ=1 AngleXU=0 Radius=1
    g18: Circle CenterX=-8.24091 CenterY=-197.481 CenterZ=0 NormalX=0 NormalY=0 NormalZ=1 AngleXU=0 Radius=1
    g19: Circle CenterX=12.8789 CenterY=-141.321 CenterZ=0 NormalX=0 NormalY=0 NormalZ=1 AngleXU=0 Radius=1
    g20: BSplineCurve PolesCount=3 KnotsCount=2 Degree=2 IsPeriodic=0
    g21: GeomPoint X=-195.441 Y=-127.082 Z=0
    g22: GeomPoint X=12.8789 Y=-141.321 Z=0
    g23: Circle CenterX=-12.8016 CenterY=-179.036 CenterZ=0 NormalX=0 NormalY=0 NormalZ=1 AngleXU=0 Radius=10.5072
    g24: Circle CenterX=0.933922 CenterY=-166.43 CenterZ=0 NormalX=0 NormalY=0 NormalZ=1 AngleXU=0 Radius=3.26661
    g25: Circle CenterX=-33.5518 CenterY=-176.44 CenterZ=0 NormalX=0 NormalY=0 NormalZ=1 AngleXU=0 Radius=5.64388
    g26: Circle CenterX=-47.2366 CenterY=-173.859 CenterZ=0 NormalX=0 NormalY=0 NormalZ=1 AngleXU=0 Radius=3.01653
    g27: Circle CenterX=-56.2595 CenterY=-171.456 CenterZ=0 NormalX=0 NormalY=0 NormalZ=1 AngleXU=0 Radius=2.12826
    g28: ArcOfCircle CenterX=51.2151 CenterY=-198.473 CenterZ=0 NormalX=0 NormalY=0 NormalZ=1 AngleXU=0 Radius=20 StartAngle=2.78189 EndAngle=4.35269
    g29: LineSegment StartX=32.4951 StartY=-191.433 StartZ=0 EndX=94.6578 EndY=-26.1352 EndZ=0
    g30: LineSegment StartX=43.1192 StartY=-220.001 StartZ=0 EndX=-196.497 EndY=-129.89 EndZ=0
    g31: LineSegment StartX=43.1192 StartY=-220.001 StartZ=0 EndX=44.1752 EndY=-217.193 EndZ=0
    g32: LineSegment StartX=117.223 StartY=-19.0875 StartZ=0 EndX=117.223 EndY=-16.0875 EndZ=0
    g33: LineSegment StartX=117.223 StartY=-16.0875 StartZ=0 EndX=17.2232 EndY=-16.0875 EndZ=0
    g34: LineSegment StartX=17.2232 StartY=-16.0875 StartZ=0 EndX=17.2232 EndY=-19.0875 EndZ=0
    g35: LineSegment StartX=28.8094 StartY=-19.0875 StartZ=0 EndX=17.2232 EndY=-19.0875 EndZ=0
    g36: LineSegment StartX=47.0443 StartY=-50.4712 StartZ=0 EndX=12.8789 EndY=-141.321 EndZ=0
    g37: LineSegment StartX=-195.441 StartY=-127.082 StartZ=0 EndX=-196.497 EndY=-129.89 EndZ=0
    g38: LineSegment StartX=85.2866 StartY=-36.8766 StartZ=0 EndX=78.9396 EndY=-53.7463 EndZ=0
    g39: LineSegment StartX=60.9579 StartY=-27.7053 StartZ=0 EndX=54.6191 EndY=-44.5532 EndZ=0
    g40: LineSegment StartX=68.0907 StartY=-82.7664 StartZ=0 EndX=61.7465 EndY=-99.6365 EndZ=0
    g41: LineSegment StartX=43.7619 StartY=-73.595 StartZ=0 EndX=37.426 EndY=-90.4435 EndZ=0
    g42: LineSegment StartX=50.885 StartY=-128.652 StartZ=0 EndX=44.5456 EndY=-145.522 EndZ=0
    g43: LineSegment StartX=26.5562 StartY=-119.481 StartZ=0 EndX=20.2251 EndY=-136.329 EndZ=0
    g44: LineSegment StartX=9.3071 StartY=-165.349 StartZ=0 EndX=2.97115 EndY=-182.197 EndZ=0
    g45: LineSegment StartX=33.6358 StartY=-174.52 StartZ=0 EndX=27.2917 EndY=-191.39 EndZ=0
  constraints (71):
    c: Block(g0)
    c: Block(g1)
    c: Block(g2)
    c: Block(g4)
    c: Block(g3)
    c: Block(g6)
    c: Block(g5)
    c: Block(g8)
    c: Block(g7)
    c: Weight(g9) = 1
    c: Equal(g9,g10)
    c: Equal(g9,g11)
    c: Equal(g9,g12)
    c: InternalAlignment(g9-g12 -> g13) x4
    c: InternalAlignment(g14,g13)
    c: InternalAlignment(g15,g13)
    c: Block(g16)
    c: Weight(g17) = 1
    c: Equal(g17,g18)
    c: Equal(g17,g19)
    c: InternalAlignment(g17,g20)
    c: InternalAlignment(g18,g20)
    c: InternalAlignment(g19,g20)
    c: InternalAlignment(g21,g20)
    c: InternalAlignment(g22,g20)
    c: Block(g20)
    c: Block(g23)
    c: Block(g24)
    c: Block(g25)
    c: Block(g26)
    c: Block(g27)
    c: Block(g28)
    c: Coincident(g29,g28)
    c: Coincident(g29,g0)
    c: Block(g13)
    c: Coincident(g31,g30)
    c: Coincident(g31,g28)
    c: Block(g31)
    c: Coincident(g32,g0)
    c: Vertical(g32)
    c: Coincident(g33,g32)
    c: Horizontal(g33)
    c: Coincident(g34,g33)
    c: Vertical(g34)
    c: Block(g33)
    c: Coincident(g35,g13)
    c: Coincident(g35,g34)
    c: Horizontal(g35)
    c: Coincident(g36,g13)
    c: Coincident(g36,g20)
    c: Coincident(g37,g20)
    c: Coincident(g37,g30)
    c: Block(g30)
    c: Coincident(g38,g1)
    c: Coincident(g38,g2)
    c: Coincident(g39,g1)
    c: Coincident(g39,g2)
    c: Coincident(g40,g3)
    c: Coincident(g40,g4)
    c: Coincident(g41,g3)
    c: Coincident(g41,g4)
    c: Coincident(g42,g5)
    c: Coincident(g42,g6)
    c: Coincident(g43,g5)
    c: Coincident(g43,g6)
    c: Coincident(g44,g7)
    c: Coincident(g44,g8)
    c: Coincident(g45,g7)
    c: Coincident(g45,g8)
    c: Distance(g30) = 256
    c: Distance(g33) = 100
FEATURE [Part::Extrusion] Extrude002
  Base = -> Sketch001
  Dir = (1,0,0)
  DirMode = 2
  FaceMakerClass = Part::FaceMakerBullseye
  LengthFwd = 8
  LengthRev = 0
  Solid = true
  Symmetric = false
FEATURE [Sketcher::SketchObject] Sketch002
  FullyConstrained = true
  sketch-geometry (20):
    g0: LineSegment StartX=-2.77179 StartY=-200.304 StartZ=0 EndX=5.22821 EndY=-200.304 EndZ=0
    g1: LineSegment StartX=5.22821 StartY=-200.304 StartZ=0 EndX=5.22821 EndY=-197.304 EndZ=0
    g2: LineSegment StartX=-2.77179 StartY=-200.304 StartZ=0 EndX=-2.77179 EndY=-197.304 EndZ=0
    g3: LineSegment StartX=5.22821 StartY=-197.304 StartZ=0 EndX=8.22821 EndY=-197.304 EndZ=0
    g4: LineSegment StartX=-2.77179 StartY=-197.304 StartZ=0 EndX=-5.77179 EndY=-197.304 EndZ=0
    g5: LineSegment StartX=19.2282 StartY=-203.304 StartZ=0 EndX=19.2282 EndY=-206.304 EndZ=0
    g6: LineSegment StartX=-16.7718 StartY=-203.304 StartZ=0 EndX=-16.7718 EndY=-206.304 EndZ=0
    g7: LineSegment StartX=-16.7718 StartY=-206.304 StartZ=0 EndX=19.2282 EndY=-206.304 EndZ=0
    g8: Circle CenterX=-16.7718 CenterY=-203.304 CenterZ=0 NormalX=0 NormalY=0 NormalZ=1 AngleXU=0 Radius=1
    g9: Circle CenterX=-5.77179 CenterY=-203.304 CenterZ=0 NormalX=0 NormalY=0 NormalZ=1 AngleXU=0 Radius=1
    g10: Circle CenterX=-5.77179 CenterY=-197.304 CenterZ=0 NormalX=0 NormalY=0 NormalZ=1 AngleXU=0 Radius=1
    g11: BSplineCurve PolesCount=3 KnotsCount=2 Degree=2 IsPeriodic=0
    g12: GeomPoint X=-16.7718 Y=-203.304 Z=0
    g13: GeomPoint X=-5.77179 Y=-197.304 Z=0
    g14: Circle CenterX=19.2282 CenterY=-203.304 CenterZ=0 NormalX=0 NormalY=0 NormalZ=1 AngleXU=0 Radius=1
    g15: Circle CenterX=8.22821 CenterY=-203.304 CenterZ=0 NormalX=0 NormalY=0 NormalZ=1 AngleXU=0 Radius=1
    g16: Circle CenterX=8.22821 CenterY=-197.304 CenterZ=0 NormalX=0 NormalY=0 NormalZ=1 AngleXU=0 Radius=1
    g17: BSplineCurve PolesCount=3 KnotsCount=2 Degree=2 IsPeriodic=0
    g18: GeomPoint X=19.2282 Y=-203.304 Z=0
    g19: GeomPoint X=8.22821 Y=-197.304 Z=0
  constraints (41):
    c: Horizontal(g0)
    c: Distance(g0) = 8
    c: Coincident(g1,g0)
    c: Vertical(g1)
    c: Distance(g1) = 3
    c: Coincident(g2,g0)
    c: Vertical(g2)
    c: Distance(g2) = 3
    c: Coincident(g3,g1)
    c: Horizontal(g3)
    c: Distance(g3) = 3
    c: Coincident(g4,g2)
    c: Horizontal(g4)
    c: Distance(g4) = 3
    c: Vertical(g5)
    c: Vertical(g6)
    c: Coincident(g7,g6)
    c: Coincident(g7,g5)
    c: Weight(g8) = 1
    c: Equal(g8,g9)
    c: Equal(g8,g10)
    c: Coincident(g11,g4)
    c: InternalAlignment(g8,g11)
    c: InternalAlignment(g9,g11)
    c: InternalAlignment(g10,g11)
    c: InternalAlignment(g12,g11)
    c: InternalAlignment(g13,g11)
    c: Coincident(g17,g5)
    c: Weight(g14) = 1
    c: Equal(g14,g15)
    c: Equal(g14,g16)
    c: Coincident(g17,g3)
    c: InternalAlignment(g14,g17)
    c: InternalAlignment(g15,g17)
    c: InternalAlignment(g16,g17)
    c: InternalAlignment(g18,g17)
    c: InternalAlignment(g19,g17)
    c: Block(g7)
    c: Block(g17)
    c: Block(g11)
    c: Block(g6)
FEATURE [Part::Extrusion] Extrude003
  Base = -> Sketch002
  Dir = (0,0,1)
  DirMode = 2
  FaceMakerClass = Part::FaceMakerBullseye
  LengthFwd = 260
  LengthRev = 0
  Solid = true
  Symmetric = false
FEATURE [Part::Extrusion] Extrude
  Base = -> Sketch
  Dir = (0,0,1)
  DirMode = 2
  FaceMakerClass = Part::FaceMakerBullseye
  LengthFwd = 14
  LengthRev = 0
  Solid = true
  Symmetric = false
